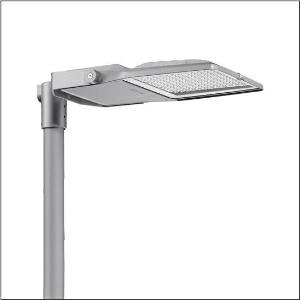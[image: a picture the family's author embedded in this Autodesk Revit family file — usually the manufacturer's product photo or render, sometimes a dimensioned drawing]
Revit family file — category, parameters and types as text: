
# Revit family: floodlight_fl_21_iq_midi___pl64_5xa7782e2e3a_fffa
name_source: partatom
category: Lighting Fixtures
units: mm (PartAtom-declared; Revit-internal decimal feet)

## family parameters
Cut with Voids When Loaded = No
Host = Face
Light Source = No
Part Type = Normal
Room Calculation Point = No
Round Connector Dimension = Use Diameter
Shared = No

## types (1)
- --- (1 x LED, 25930 lm, 208.1 W, 3000K)
    Apparent Load = 208 VA
    CIE Flux Codes = 28 80 98 100 100
    Color Rendering = 70
    Color Temperature = 3000K
    Default Elevation = 1800 mm
    Description = Floodlight FL 21 iQ midi, floodlight, primary light control with lens, of PMMA, primary optical cover: protective disc, of toughened safety glass, transparent, light distribution: PL64, light emission: direct distribution, installation type: surface-mounted, LED, High Power LED, rated luminous flux: 25.930lm, luminous efficacy: 125lm/W, light colour: 730, colour temperature: 3000K, control gear: ECG iQ, control: optimised constant luminous flux control (CLO 2.0), Desk-Remote (wireless, voltage-free reading and setting of iQ features in the workshop via application-optimized NFC function/RFID function), Smart-Wire, Night-Set, Temp-Guard, Auto-Match, Street-Remote, with terminal, 6-pole, mains connection: 220..240V, AC, 50/60Hz, start of lifetime: 208W, end of service life: 227W, reduction: 90W, luminaire housing, of diecast aluminium, powder-coated, Siteco® metallic grey (DB 702S), corrosivity category C5 mid according to DIN EN ISO 12944, sealing non-destructively replaceable, please order mast flange separately, mast bracket, of steel, galvanised, powder-coated, Siteco® metallic grey (DB 702S), protection rating (complete): IP66, insulation class (complete): insulation class II (safety insulation), certification: CE, ENEC, VDE, protection symbol: D, impact resistance: IK08, permissible operating ambient temperature: -40..+40°C, permissible operating ambient temperature for outdoor applications: -40..+50°C, standard: DIN EN 12944, LABS conformity tested according to VDMA 24364:2018-05, packaging unit: 1 piece

Light Distribution: PL64
    Height = 76 mm
    Lamp = 1 x LED
    Lamp Light Flux = 25930 lm
    Lamp Power = 208.1 W
    Lamp count = 1
    Length = 657 mm
    Luminous efficacy = 125 lm/W
    Manufacturer = Siteco
    ModVariant = No
    Model = 5XA7782E2E3A
    Number of Poles = 1
    OnlyDefault = Yes
    Power Factor = 1
    Product Name = Floodlight FL 21 iQ midi | PL64
    Product group = floodlight | pylon annexe
    ProductGroupID = 6200
    Protection Class = Protection class II
    Protection Degree = IP 66
    RLX_Detail_Level = 1
    RLX_Emergency_Light_Flux = 0 lm
    RLX_Emergency_Type = 0
    RLX_Emergency_Type_DB = No
    RlxData = <blob elided: 153737 chars, md5=a1117a4c>
    Socket = socket
    Standby Power = 0 W
    System Light Flux = 25930 lm
    System Power = 208 W
    Type Comments = factory setting: luminous flux: 100 % | dim-lin: 254 | 710 mA
    Type Image = l_1007123.jpg
    URL = http://relux.com
    VarID = @adj_075943
    Voltage = 0 V
    Weight = 0.00 kg
    Width = 442 mm

## geometry (parser evidence)
native form markers: Blend x4, Sweep x13
no freeform markers — native parametric forms only
